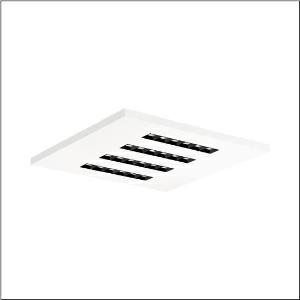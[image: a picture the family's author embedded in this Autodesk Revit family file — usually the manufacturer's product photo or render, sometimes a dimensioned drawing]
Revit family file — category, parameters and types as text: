
# Revit family: silica_r__21_square_51mx6kds34w_2a5b
name_source: partatom
category: Lighting Fixtures
units: mm (PartAtom-declared; Revit-internal decimal feet)

## family parameters
Cut with Voids When Loaded = No
Host = Face
Light Source = No
Part Type = Normal
Room Calculation Point = No
Round Connector Dimension = Use Diameter
Shared = No

## types (1)
- --- (1 x LED, 4600 lm, 31.9 W, 3000K)
    Apparent Load = 32 VA
    CIE Flux Codes = 86 100 100 100 100
    Color Rendering = 80
    Color Temperature = 3000K
    Default Elevation = 1800 mm
    Description = Silica® 21 Square, office luminaire, primary light control with lens, of PMMA, primary anti-glare with reflector, of PC, black, CAT 2 (L<= 3000cd/m²), light emission: direct distribution, primary light characteristic: symmetric, installation type: lay-in mounting, LED, rated luminous flux: 4.600lm, luminous efficacy: 144lm/W, light colour: 830, colour temperature: 3000K, with terminal, 5-pole, mains connection: 220..240V, AC, 50/60Hz, rated input power: 31.9W, luminaire housing, of sheet steel, coated, traffic white (RAL 9016), module: M600, length: 597mm, width: 597mm, height: 33mm, protection rating (complete): IP20, insulation class (complete): insulation class I (protective earthing), certification: CE, permissible operating ambient temperature: -20..+40°C, standard: EN 50419, packaging unit: 1 piece
    Height = 0 mm  [stored 0 ft]
    Lamp = 1 x LED
    Lamp Light Flux = 4600 lm
    Lamp Power = 31.9 W
    Lamp count = 1
    Length = 597 mm
    Luminous efficacy = 144 lm/W
    Manufacturer = Siteco
    ModVariant = No
    Model = 51MX6KDS34W
    Mounting Place = Ceiling
    Mounting Type = Recessed
    Number of Poles = 1
    OnlyDefault = Yes
    Power Factor = 1
    Product Name = Silica® 21 Square
    Product group = office luminaire | ceiling recessed
    ProductGroupID = 401
    Protection Class = Protection class I
    Protection Degree = IP 20
    RLX_Detail_Level = 1
    RLX_Emergency_Light_Flux = 0 lm
    RLX_Emergency_Type = 0
    RLX_Emergency_Type_DB = No
    RlxData = <blob elided: 21081 chars, md5=0c4c5d20>
    Socket = socket
    Standby Power = 0 W
    System Light Flux = 4600 lm
    System Power = 32 W
    Type Comments = factory setting: luminous flux: 100 % | dim-lin: 254 | 430 mA
    Type Image = l_1275207.jpg
    URL = http://relux.com
    VarID = @adj_036385
    Voltage = 0 V
    Weight = 0.00 kg
    Width = 597 mm

note: [stored X ft] marks values corroborated as IEEE doubles in the binary element streams (Revit-internal decimal feet)

## geometry (parser evidence)
native form markers: Blend x4, Sweep x10
no freeform markers — native parametric forms only
